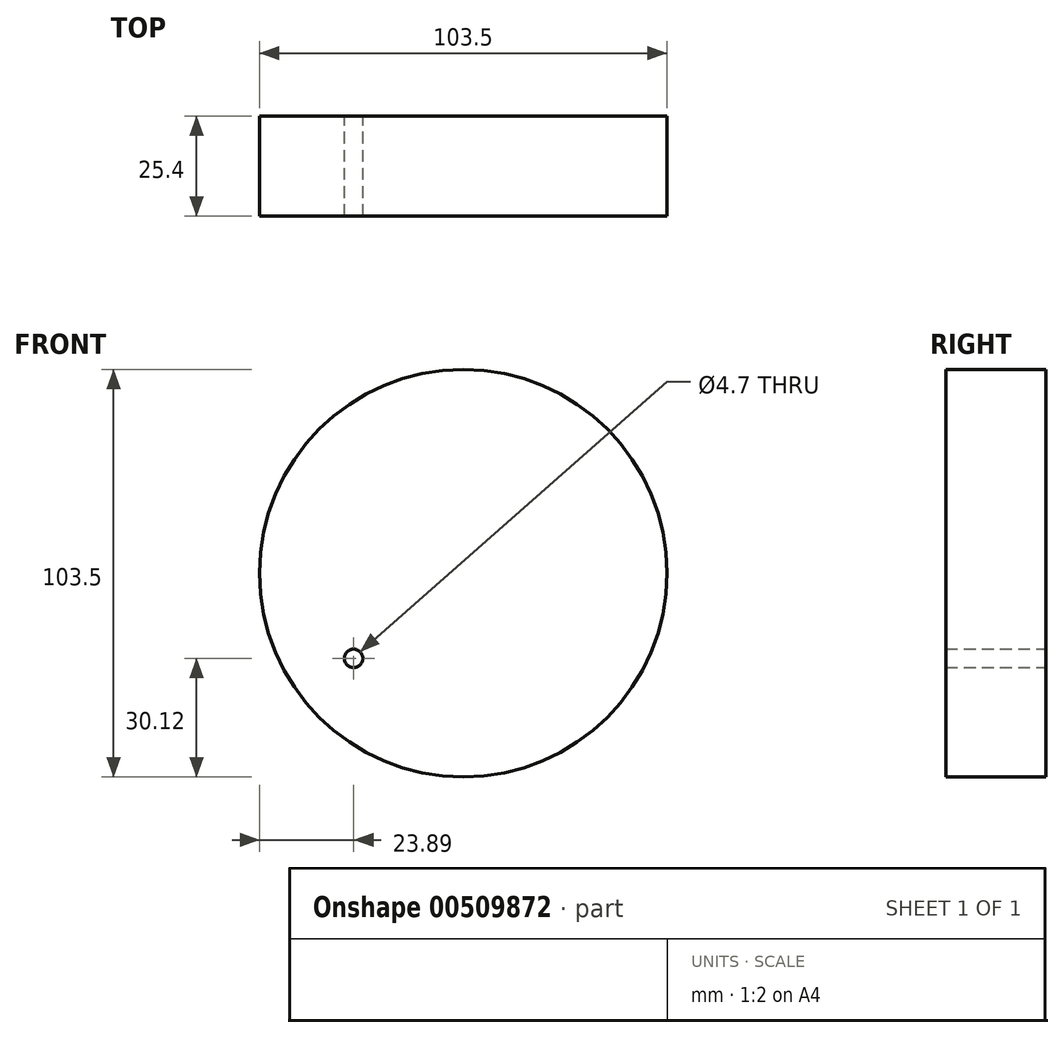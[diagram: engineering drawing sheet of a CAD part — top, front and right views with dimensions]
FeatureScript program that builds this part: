
annotation { "Feature Type Name" : "Feature", "Feature Type Description" : "" }
export const myFeature = defineFeature(function(context is Context, id is Id, definition is map)
    precondition{}
    {
        {
            var Q0;
            Q0=qCreatedBy(makeId("Front.planeOp"),FACE);
            var sketch = newSketch(context, id + "F0", { "sketchPlane" : qUnion([Q0])});
            skCircle(sketch, "E0", {"center": v(0, 0) * mm, "radius": 2.35 * mm});
            skCircle(sketch, "E1", {"center": v(27.86, 21.63) * mm, "radius": 51.75 * mm});
            skSolve(sketch);
        }
        {
            var Q0;
            Q0 = qSketchRegion(id + "F0", true);
            extrude(context, id + "F1", {"entities" : qUnion([Q0]), "depth" : 25.4 * mm});
        }
    });
